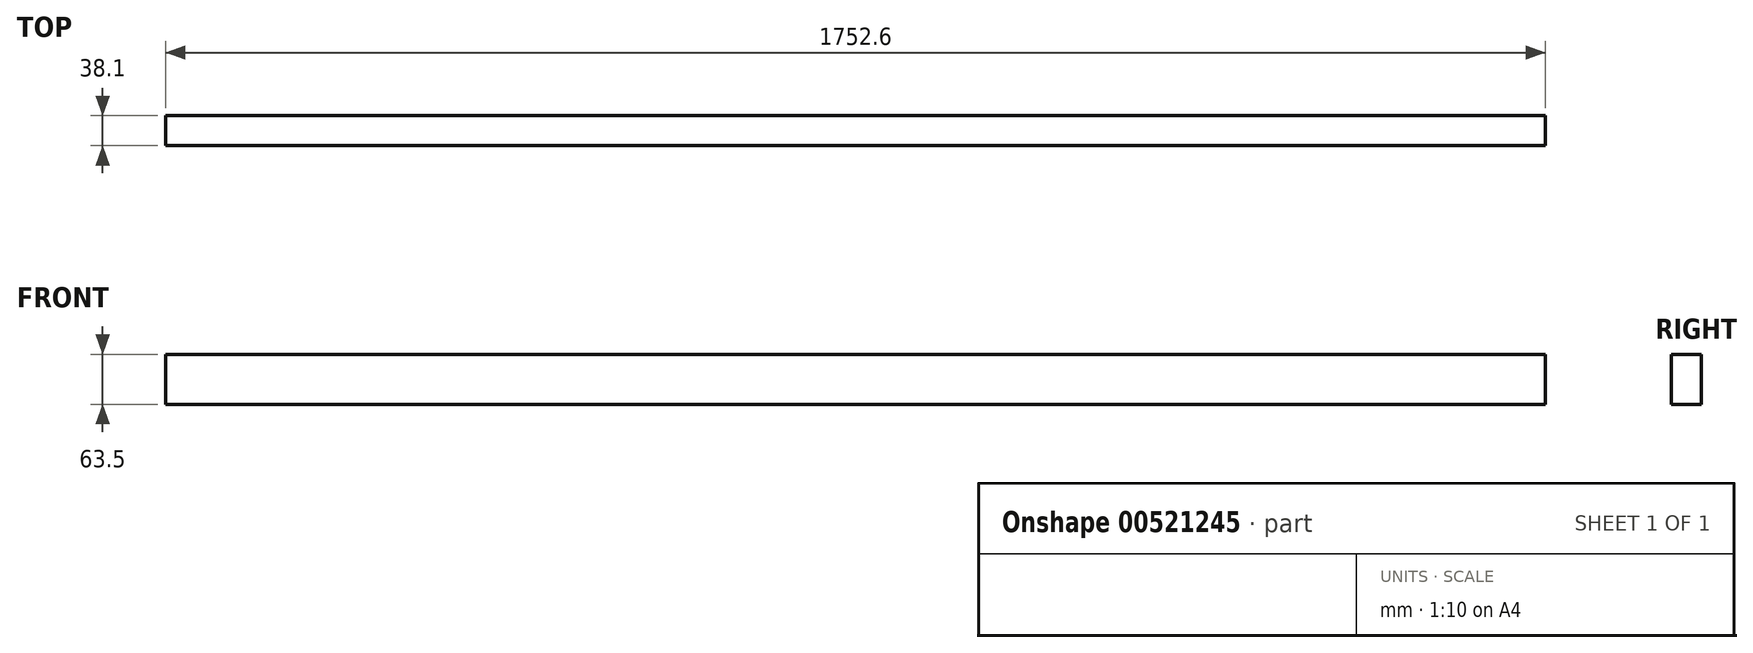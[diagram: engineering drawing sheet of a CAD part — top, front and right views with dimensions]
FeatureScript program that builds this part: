
annotation { "Feature Type Name" : "Feature", "Feature Type Description" : "" }
export const myFeature = defineFeature(function(context is Context, id is Id, definition is map)
    precondition{}
    {
        {
            var Q0;
            Q0=qCreatedBy(makeId("Front.planeOp"),FACE);
            var sketch = newSketch(context, id + "F0", { "sketchPlane" : qUnion([Q0])});
            skLineSegment(sketch, "E0.bottom", {"start": v(-876.3, 63.5) * mm, "end": v(876.3, 63.5) * mm});
            skLineSegment(sketch, "E0.top", {"start": v(-876.3, 0) * mm, "end": v(876.3, 0) * mm});
            skLineSegment(sketch, "E0.left", {"start": v(-876.3, 63.5) * mm, "end": v(-876.3, 0) * mm});
            skLineSegment(sketch, "E0.right", {"start": v(876.3, 63.5) * mm, "end": v(876.3, 0) * mm});
            skLineSegment(sketch, "E1", {"start": v(0, 58.07) * mm, "end": v(0, -50.51) * mm});
            skSolve(sketch);
        }
        {
            var Q0;
            Q0=makeQuery(id+"F0.imprint","IMPRINT",FACE,{"disambiguationData":[TD([[makeQuery(id+"F0.imprint","IMPRINT",EDGE,{"derivedFrom":sQuery(id+"F0.wireOp",EDGE,"E0.bottom")}),-1.0]])]});
            extrude(context, id + "F1", {"entities" : qUnion([Q0]), "depth" : 38.1 * mm, "offsetDistance" : 25.4 * mm});
        }
    });
